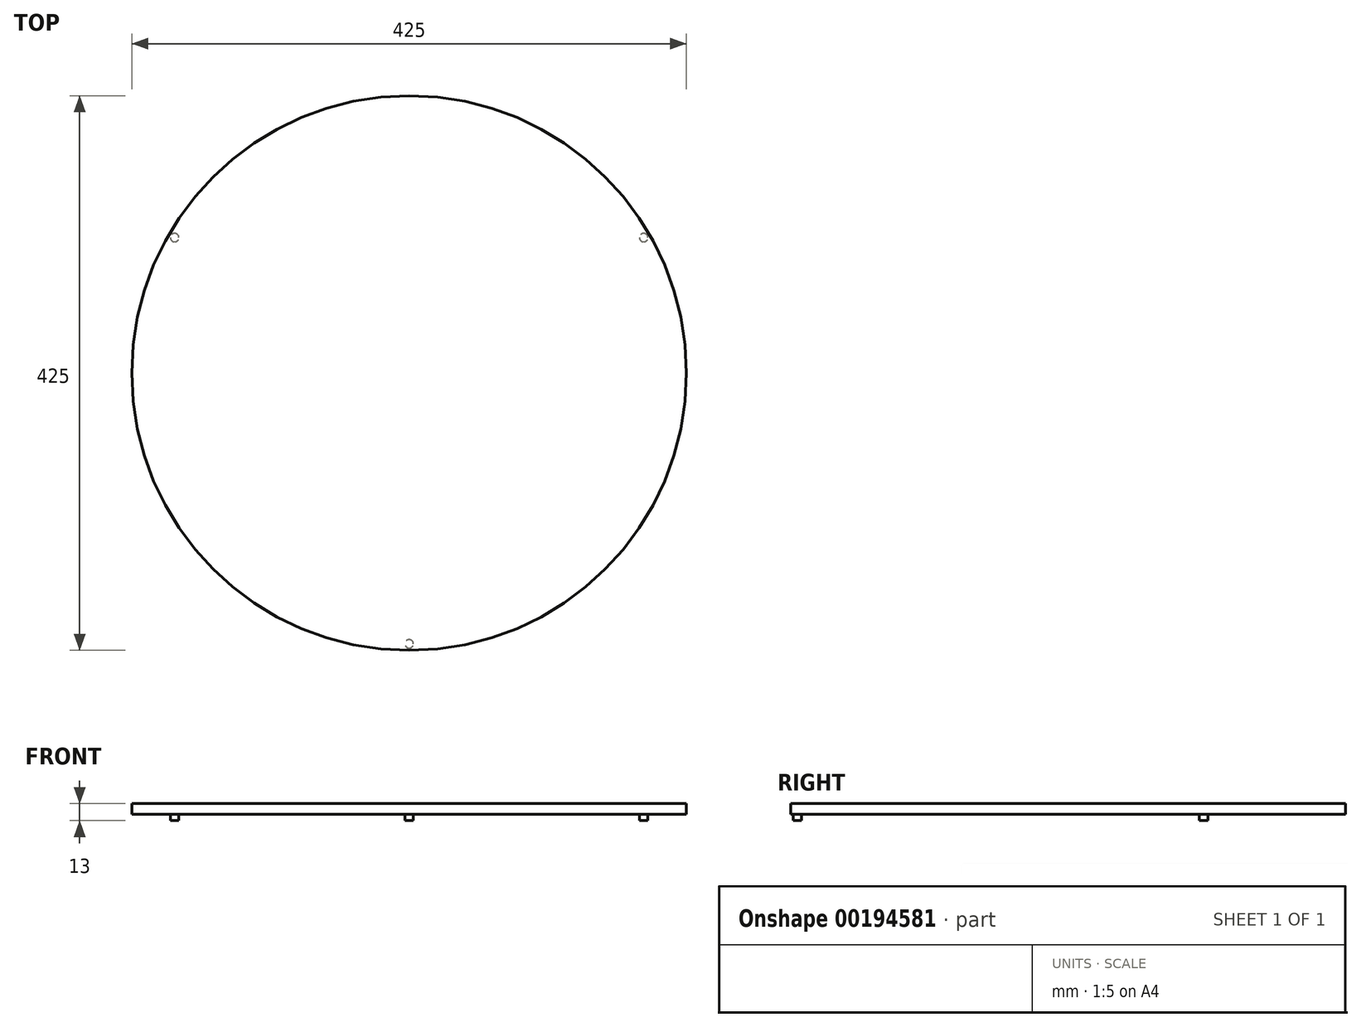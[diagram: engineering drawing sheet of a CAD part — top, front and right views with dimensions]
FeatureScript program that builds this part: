
annotation { "Feature Type Name" : "Feature", "Feature Type Description" : "" }
export const myFeature = defineFeature(function(context is Context, id is Id, definition is map)
    precondition{}
    {
        {
            var Q0;
            Q0=qCreatedBy(makeId("Top.planeOp"),FACE);
            var sketch = newSketch(context, id + "F0", { "sketchPlane" : qUnion([Q0])});
            skCircle(sketch, "E0", {"center": v(0, 0) * mm, "radius": 212.5 * mm});
            skSolve(sketch);
        }
        {
            var Q0;
            Q0 = qSketchRegion(id + "F0", true);
            extrude(context, id + "F1", {"entities" : qUnion([Q0]), "depth" : 8 * mm});
        }
        {
            var Q0;
            Q0=makeQuery(id+"F1.opExtrude","CAP_FACE",FACE,{"disambiguationData":[OSD([sQuery(id+"F0.wireOp",EDGE,"E0")])],"isStart":true});
            var sketch = newSketch(context, id + "F2", { "sketchPlane" : qUnion([Q0])});
            skCircle(sketch, "E1", {"center": v(0, 207.5) * mm, "radius": 3.25 * mm});
            skPoint(sketch, "E2.center", {"position": v(0, 0) * mm});
            skCircle(sketch, "E3.1.0", {"center": v(-179.7, -103.75) * mm, "radius": 3.25 * mm});
            skCircle(sketch, "E3.2.0", {"center": v(179.7, -103.75) * mm, "radius": 3.25 * mm});
            skSolve(sketch);
        }
        {
            var Q0;
            Q0 = qSketchRegion(id + "F2", true);
            extrude(context, id + "F3", {"entities" : qUnion([Q0]), "operationType" : NewBodyOperationType.ADD, "depth" : 5 * mm});
        }
    });
